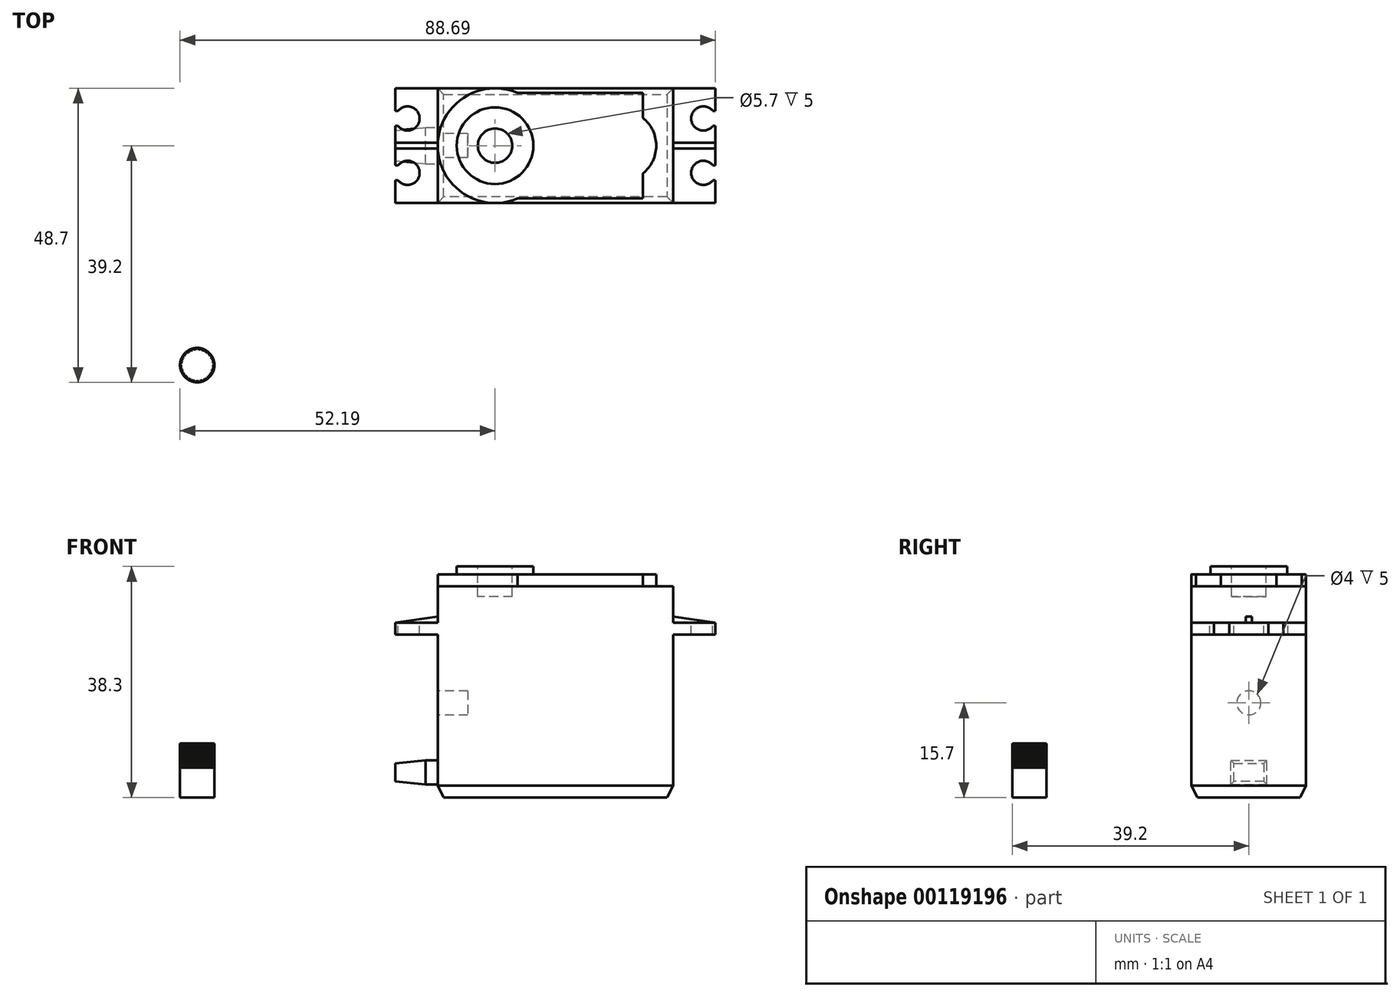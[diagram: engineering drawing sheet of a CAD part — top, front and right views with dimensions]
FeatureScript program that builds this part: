
annotation { "Feature Type Name" : "Feature", "Feature Type Description" : "" }
export const myFeature = defineFeature(function(context is Context, id is Id, definition is map)
    precondition{}
    {
        {
            var Q0;
            Q0=qCreatedBy(makeId("Top.planeOp"),FACE);
            var sketch = newSketch(context, id + "F0", { "sketchPlane" : qUnion([Q0])});
            skLineSegment(sketch, "E0.bottom", {"start": v(19.5, -9.5) * mm, "end": v(-19.5, -9.5) * mm});
            skLineSegment(sketch, "E0.top", {"start": v(19.5, 9.5) * mm, "end": v(-19.5, 9.5) * mm});
            skLineSegment(sketch, "E0.left", {"start": v(19.5, -9.5) * mm, "end": v(19.5, 9.5) * mm});
            skLineSegment(sketch, "E0.right", {"start": v(-19.5, -9.5) * mm, "end": v(-19.5, 9.5) * mm});
            skPoint(sketch, "E0.middle", {"position": v(0, 0) * mm});
            skSolve(sketch);
        }
        {
            var Q0;
            Q0 = qSketchRegion(id + "F0", true);
            extrude(context, id + "F1", {"entities" : qUnion([Q0]), "depth" : 35 * mm});
        }
        {
            var Q0;
            Q0=makeQuery(id+"F1.opExtrude","SWEPT_FACE",FACE,{"disambiguationData":[OSD([sQuery(id+"F0.wireOp",EDGE,"E0.right")])]});
            var sketch = newSketch(context, id + "F2", { "sketchPlane" : qUnion([Q0])});
            skLineSegment(sketch, "E1", {"start": v(-9.5, 29) * mm, "end": v(9.5, 29) * mm});
            skLineSegment(sketch, "E2", {"start": v(-9.5, 27) * mm, "end": v(9.5, 27) * mm});
            skSolve(sketch);
        }
        {
            var Q0;
            {var subQ0=sQuery(id+"F2.wireOp",EDGE,"E1");Q0=makeQuery(id+"F2.imprint","IMPRINT",FACE,{"disambiguationData":[TD([[makeQuery(id+"F2.imprint","IMPRINT",EDGE,{"derivedFrom":subQ0}),-1.0]])]});}
            extrude(context, id + "F3", {"entities" : qUnion([Q0]), "operationType" : NewBodyOperationType.ADD, "depth" : 7 * mm});
        }
        {
            var Q0;
            Q0=makeQuery(id+"F3.opExtrude","SWEPT_FACE",FACE,{"disambiguationData":[OSD([sQuery(id+"F2.wireOp",EDGE,"E1")])]});
            var sketch = newSketch(context, id + "F4", { "sketchPlane" : qUnion([Q0])});
            skLineSegment(sketch, "E3", {"start": v(-26.5, 0.5) * mm, "end": v(-19.5, 0.5) * mm});
            skLineSegment(sketch, "E4", {"start": v(-26.5, -0.5) * mm, "end": v(-19.5, -0.5) * mm});
            skSolve(sketch);
        }
        {
            var Q0;
            {var subQ0=sQuery(id+"F4.wireOp",EDGE,"E3");Q0=makeQuery(id+"F4.imprint","IMPRINT",FACE,{"disambiguationData":[TD([[makeQuery(id+"F4.imprint","IMPRINT",EDGE,{"derivedFrom":subQ0}),-1.0]])]});}
            extrude(context, id + "F5", {"entities" : qUnion([Q0]), "operationType" : NewBodyOperationType.ADD, "depth" : 1 * mm});
        }
        {
            var Q0;
            Q0=makeQuery(id+"F5.opExtrude","SWEPT_FACE",FACE,{"disambiguationData":[OSD([sQuery(id+"F4.wireOp",EDGE,"E4")])]});
            var sketch = newSketch(context, id + "F6", { "sketchPlane" : qUnion([Q0])});
            skLineSegment(sketch, "E5", {"start": v(-26.5, 29) * mm, "end": v(-19.5, 30) * mm});
            skSolve(sketch);
        }
        {
            var Q0;
            Q0=makeQuery(id+"F6.imprint","IMPRINT",FACE,{"disambiguationData":[TD([[makeQuery(id+"F6.imprint","IMPRINT",EDGE,{"derivedFrom":sQuery(id+"F6.wireOp",EDGE,"E5")}),1.0]])]});
            extrude(context, id + "F7", {"entities" : qUnion([Q0]), "operationType" : NewBodyOperationType.REMOVE, "endBound" : BoundingType.UP_TO_NEXT, "oppositeDirection" : true, "depth" : 25 * mm});
        }
        {
            var Q0;
            Q0=makeQuery(id+"F1.opExtrude","CAP_FACE",FACE,{"disambiguationData":[OSD([sQuery(id+"F0.wireOp",EDGE,"E0.bottom"),sQuery(id+"F0.wireOp",EDGE,"E0.top"),sQuery(id+"F0.wireOp",EDGE,"E0.left"),sQuery(id+"F0.wireOp",EDGE,"E0.right")])],"isStart":true});
            chamfer(context, id + "F8", {"entities" : qUnion([Q0]), "chamferType" : ChamferType.TWO_OFFSETS, "width1" : 1 * mm, "oppositeDirection" : false, "width2" : 2 * mm, "tangentPropagation" : true});
        }
        {
            var Q0;
            {var subQ1=sQuery(id+"F0.wireOp",EDGE,"E0.bottom");var subQ2=sQuery(id+"F2.wireOp",EDGE,"E1");Q0=makeQuery(id+"F5.boolean.opBoolean","SPLIT",FACE,{"disambiguationData":[TD([makeQuery(id+"F1.opExtrude","SWEPT_FACE",FACE,{"disambiguationData":[OSD([subQ1])]})])],"derivedFrom":makeQuery(id+"F3.opExtrude","SWEPT_FACE",FACE,{"disambiguationData":[OSD([subQ2])]})});}
            var sketch = newSketch(context, id + "F9", { "sketchPlane" : qUnion([Q0])});
            skArc(sketch, "E6", {"start": v(-26.06, 3.25) * mm, "mid": v(-22.5, 4.5) * mm, "end": v(-26.06, 5.75) * mm});
            skLineSegment(sketch, "E7", {"start": v(-26.06, 5.75) * mm, "end": v(-26.06, 3.25) * mm});
            skLineSegment(sketch, "E8.bottom", {"start": v(-26.06, 5.75) * mm, "end": v(-26.56, 5.75) * mm});
            skLineSegment(sketch, "E8.top", {"start": v(-26.06, 3.25) * mm, "end": v(-26.56, 3.25) * mm});
            skLineSegment(sketch, "E8.right", {"start": v(-26.56, 5.75) * mm, "end": v(-26.56, 3.25) * mm});
            skLineSegment(sketch, "E9.MirrorCS", {"start": v(-26.56, -5.75) * mm, "end": v(-26.56, -3.25) * mm});
            skLineSegment(sketch, "E10.MirrorCS", {"start": v(-26.06, -5.75) * mm, "end": v(-26.56, -5.75) * mm});
            skLineSegment(sketch, "E11.MirrorCS", {"start": v(-26.06, -5.75) * mm, "end": v(-26.06, -3.25) * mm});
            skLineSegment(sketch, "E12.MirrorCS", {"start": v(-26.06, -3.25) * mm, "end": v(-26.56, -3.25) * mm});
            skArc(sketch, "E13.MirrorCS", {"start": v(-26.06, -3.25) * mm, "mid": v(-22.5, -4.5) * mm, "end": v(-26.06, -5.75) * mm});
            skSolve(sketch);
        }
        {
            var Q0;
            Q0=makeQuery(id+"F9.imprint","IMPRINT",FACE,{"disambiguationData":[TD([[makeQuery(id+"F9.imprint","IMPRINT",EDGE,{"derivedFrom":sQuery(id+"F9.wireOp",EDGE,"E8.bottom")}),1.0]])]});
            var Q1;
            Q1=makeQuery(id+"F9.imprint","IMPRINT",FACE,{"disambiguationData":[TD([[makeQuery(id+"F9.imprint","IMPRINT",EDGE,{"derivedFrom":sQuery(id+"F9.wireOp",EDGE,"E6")}),1.0]])]});
            var Q2;
            {var subQ1=sQuery(id+"F9.wireOp",EDGE,"E11.MirrorCS");Q2=makeQuery(id+"F9.imprint","IMPRINT",FACE,{"disambiguationData":[TD([[makeQuery(id+"F9.imprint","IMPRINT",EDGE,{"derivedFrom":subQ1}),1.0]])]});}
            var Q3;
            Q3=makeQuery(id+"F9.imprint","IMPRINT",FACE,{"disambiguationData":[TD([[makeQuery(id+"F9.imprint","IMPRINT",EDGE,{"derivedFrom":sQuery(id+"F9.wireOp",EDGE,"E11.MirrorCS")}),-1.0]])]});
            extrude(context, id + "F10", {"entities" : qUnion([Q0, Q1, Q2, Q3]), "operationType" : NewBodyOperationType.REMOVE, "endBound" : BoundingType.UP_TO_NEXT, "oppositeDirection" : true, "depth" : 25 * mm});
        }
        {
            var Q0;
            Q0=makeQuery(id+"F1.opExtrude","SWEPT_BODY",BODY,{"disambiguationData":[OSD([sQuery(id+"F0.wireOp",EDGE,"E0.bottom"),sQuery(id+"F0.wireOp",EDGE,"E0.top"),sQuery(id+"F0.wireOp",EDGE,"E0.left"),sQuery(id+"F0.wireOp",EDGE,"E0.right")])]});
            var Q1;
            Q1=qCreatedBy(makeId("Right.planeOp"),FACE);
            mirror(context, id + "F11", {"operationType" : NewBodyOperationType.ADD, "entities" : qUnion([Q0]), "mirrorPlane" : qUnion([Q1])});
        }
        {
            var Q0;
            {var subQ1=sQuery(id+"F0.wireOp",EDGE,"E0.right");Q0=makeQuery(id+"F3.boolean.opBoolean","SPLIT",FACE,{"disambiguationData":[TD([makeQuery(id+"F3.opExtrude","SWEPT_FACE",FACE,{"disambiguationData":[OSD([sQuery(id+"F2.wireOp",EDGE,"E2")])]})])],"derivedFrom":makeQuery(id+"F1.opExtrude","SWEPT_FACE",FACE,{"disambiguationData":[OSD([subQ1])]})});}
            var sketch = newSketch(context, id + "F12", { "sketchPlane" : qUnion([Q0])});
            skLineSegment(sketch, "E14.bottom", {"start": v(3, 2.2) * mm, "end": v(-3, 2.2) * mm});
            skLineSegment(sketch, "E14.top", {"start": v(3, 6.2) * mm, "end": v(-3, 6.2) * mm});
            skLineSegment(sketch, "E14.left", {"start": v(3, 2.2) * mm, "end": v(3, 6.2) * mm});
            skLineSegment(sketch, "E14.right", {"start": v(-3, 2.2) * mm, "end": v(-3, 6.2) * mm});
            skPoint(sketch, "E14.middle", {"position": v(0, 4.2) * mm});
            skCircle(sketch, "E15", {"center": v(0, 15.7) * mm, "radius": 2 * mm});
            skSolve(sketch);
        }
        {
            var Q0;
            Q0=makeQuery(id+"F12.imprint","IMPRINT",FACE,{"disambiguationData":[TD([[makeQuery(id+"F12.imprint","IMPRINT",EDGE,{"derivedFrom":sQuery(id+"F12.wireOp",EDGE,"E14.bottom")}),-1.0]])]});
            extrude(context, id + "F13", {"entities" : qUnion([Q0]), "operationType" : NewBodyOperationType.ADD, "depth" : 7 * mm});
        }
        {
            var Q0;
            Q0=makeQuery(id+"F12.imprint","IMPRINT",FACE,{"disambiguationData":[TD([[makeQuery(id+"F12.imprint","IMPRINT",EDGE,{"derivedFrom":sQuery(id+"F12.wireOp",EDGE,"E15")}),1.0]])]});
            extrude(context, id + "F14", {"entities" : qUnion([Q0]), "operationType" : NewBodyOperationType.REMOVE, "oppositeDirection" : true, "depth" : 5 * mm});
        }
        {
            var Q0;
            Q0=makeQuery(id+"F13.opExtrude","CAP_FACE",FACE,{"disambiguationData":[OSD([sQuery(id+"F12.wireOp",EDGE,"E14.bottom"),sQuery(id+"F12.wireOp",EDGE,"E14.top"),sQuery(id+"F12.wireOp",EDGE,"E14.left"),sQuery(id+"F12.wireOp",EDGE,"E14.right")])],"isStart":false});
            chamfer(context, id + "F15", {"entities" : qUnion([Q0]), "chamferType" : ChamferType.TWO_OFFSETS, "width1" : 5 * mm, "oppositeDirection" : false, "width2" : 0.5 * mm, "tangentPropagation" : true});
        }
        {
            var Q0;
            Q0=makeQuery(id+"F1.opExtrude","CAP_FACE",FACE,{"disambiguationData":[OSD([sQuery(id+"F0.wireOp",EDGE,"E0.bottom"),sQuery(id+"F0.wireOp",EDGE,"E0.top"),sQuery(id+"F0.wireOp",EDGE,"E0.left"),sQuery(id+"F0.wireOp",EDGE,"E0.right")])],"isStart":false});
            var sketch = newSketch(context, id + "F16", { "sketchPlane" : qUnion([Q0])});
            skCircle(sketch, "E16", {"center": v(-10, 0) * mm, "radius": 9.5 * mm});
            skPoint(sketch, "E16.first.point", {"position": v(-10, 9.5) * mm});
            skPoint(sketch, "E16.second.point", {"position": v(-19.5, 0) * mm});
            skPoint(sketch, "E16.third.point", {"position": v(-10, -9.5) * mm});
            skLineSegment(sketch, "E17", {"start": v(14.5, 8.75) * mm, "end": v(14.5, -8.75) * mm});
            skLineSegment(sketch, "E18", {"start": v(14.5, -8.75) * mm, "end": v(-6.3, -8.75) * mm});
            skLineSegment(sketch, "E19", {"start": v(14.5, 8.75) * mm, "end": v(-6.3, 8.75) * mm});
            skCircle(sketch, "E20", {"center": v(10.8, 0) * mm, "radius": 5.9 * mm});
            skPoint(sketch, "E20.first.point", {"position": v(14.5, 4.6) * mm});
            skPoint(sketch, "E20.second.point", {"position": v(14.5, -4.6) * mm});
            skPoint(sketch, "E20.third.point", {"position": v(16.7, 0) * mm});
            skPoint(sketch, "E20.third.point.positionSnap0", {"position": v(19.5, 0) * mm});
            skCircle(sketch, "E21", {"center": v(-10, 0) * mm, "radius": 6.35 * mm});
            skSolve(sketch);
        }
        {
            var Q0;
            {var subQ0=sQuery(id+"F16.wireOp",EDGE,"E16");var subQ5=makeQuery(id+"F16.imprint","INTERSECT",VERTEX,{"derivedFrom":[subQ0,sQuery(id+"F16.wireOp",EDGE,"E19")]});Q0=makeQuery(id+"F16.imprint","IMPRINT",FACE,{"disambiguationData":[TD([[makeQuery(id+"F16.imprint","IMPRINT",EDGE,{"disambiguationData":[TD([[subQ5,-1.0]])],"derivedFrom":subQ0}),1.0]])]});}
            var Q1;
            {var subQ0=sQuery(id+"F16.wireOp",EDGE,"E18");Q1=makeQuery(id+"F16.imprint","IMPRINT",FACE,{"disambiguationData":[TD([[makeQuery(id+"F16.imprint","IMPRINT",EDGE,{"derivedFrom":subQ0}),-1.0]])]});}
            var Q2;
            {var subQ0=sQuery(id+"F16.wireOp",EDGE,"E20");var subQ1=sQuery(id+"F16.wireOp",EDGE,"E17");var subQ2=makeQuery(id+"F16.imprint","INTERSECT",VERTEX,{"disambiguationData":[OD(0.0)],"derivedFrom":[subQ1,subQ0]});Q2=makeQuery(id+"F16.imprint","IMPRINT",FACE,{"disambiguationData":[TD([[makeQuery(id+"F16.imprint","IMPRINT",EDGE,{"disambiguationData":[TD([[subQ2,-1.0]])],"derivedFrom":subQ1}),-1.0]])]});}
            var Q3;
            {var subQ0=sQuery(id+"F16.wireOp",EDGE,"E20");var subQ1=sQuery(id+"F16.wireOp",EDGE,"E17");var subQ2=makeQuery(id+"F16.imprint","INTERSECT",VERTEX,{"disambiguationData":[OD(0.0)],"derivedFrom":[subQ1,subQ0]});Q3=makeQuery(id+"F16.imprint","IMPRINT",FACE,{"disambiguationData":[TD([[makeQuery(id+"F16.imprint","IMPRINT",EDGE,{"disambiguationData":[TD([[subQ2,-1.0]])],"derivedFrom":subQ1}),1.0]])]});}
            extrude(context, id + "F17", {"entities" : qUnion([Q0, Q1, Q2, Q3]), "operationType" : NewBodyOperationType.ADD, "depth" : 2 * mm});
        }
        {
            var Q0;
            Q0=makeQuery(id+"F17.boolean.opBoolean","SPLIT",FACE,{"disambiguationData":[TD([makeQuery(id+"F17.opExtrude","SWEPT_FACE",FACE,{"disambiguationData":[OSD([sQuery(id+"F16.wireOp",EDGE,"E21")])]})])],"derivedFrom":makeQuery(id+"F1.opExtrude","CAP_FACE",FACE,{"disambiguationData":[OSD([sQuery(id+"F0.wireOp",EDGE,"E0.bottom"),sQuery(id+"F0.wireOp",EDGE,"E0.top"),sQuery(id+"F0.wireOp",EDGE,"E0.left"),sQuery(id+"F0.wireOp",EDGE,"E0.right")])],"isStart":false})});
            extrude(context, id + "F18", {"entities" : qUnion([Q0]), "operationType" : NewBodyOperationType.ADD, "depth" : 3.3 * mm});
        }
        {
            var Q0;
            Q0=makeQuery(id+"F18.opExtrude","CAP_FACE",FACE,{"disambiguationData":[OSD([sQuery(id+"F0.wireOp",EDGE,"E0.bottom"),sQuery(id+"F0.wireOp",EDGE,"E0.top"),sQuery(id+"F0.wireOp",EDGE,"E0.left"),sQuery(id+"F0.wireOp",EDGE,"E0.right")])],"isStart":false});
            var sketch = newSketch(context, id + "F19", { "sketchPlane" : qUnion([Q0])});
            skCircle(sketch, "E22", {"center": v(-10, 0) * mm, "radius": 2.85 * mm});
            skSolve(sketch);
        }
        {
            var Q0;
            Q0 = qSketchRegion(id + "F19", true);
            extrude(context, id + "F20", {"entities" : qUnion([Q0]), "operationType" : NewBodyOperationType.REMOVE, "oppositeDirection" : true, "depth" : 5 * mm});
        }
        {
            var Q0;
            Q0=qCreatedBy(makeId("Top.planeOp"),FACE);
            var sketch = newSketch(context, id + "F21", { "sketchPlane" : qUnion([Q0])});
            skCircle(sketch, "E23", {"center": v(-59.34, -36.35) * mm, "radius": 2.85 * mm});
            skSolve(sketch);
        }
        {
            var Q0;
            Q0 = qSketchRegion(id + "F21", true);
            extrude(context, id + "F22", {"entities" : qUnion([Q0]), "depth" : 5 * mm});
        }
        {
            var Q0;
            Q0=makeQuery(id+"F22.opExtrude","CAP_FACE",FACE,{"disambiguationData":[OSD([sQuery(id+"F21.wireOp",EDGE,"E23")])],"isStart":false});
            var sketch = newSketch(context, id + "F23", { "sketchPlane" : qUnion([Q0])});
            skArc(sketch, "E24", {"start": v(-60.84, -34.29) * mm, "mid": v(-60.84, -34.29) * mm, "end": v(-60.84, -34.29) * mm});
            skLineSegment(sketch, "E25", {"start": v(-59.66, -33.82) * mm, "end": v(-59.34, -33.5) * mm});
            skLineSegment(sketch, "E26", {"start": v(-59.34, -33.5) * mm, "end": v(-59.02, -33.82) * mm});
            skLineSegment(sketch, "E27.1.0", {"start": v(-60.28, -33.98) * mm, "end": v(-60.05, -33.59) * mm});
            skLineSegment(sketch, "E27.1.1", {"start": v(-60.05, -33.59) * mm, "end": v(-59.66, -33.82) * mm});
            skLineSegment(sketch, "E27.2.0", {"start": v(-60.84, -34.29) * mm, "end": v(-60.71, -33.85) * mm});
            skLineSegment(sketch, "E27.2.1", {"start": v(-60.71, -33.85) * mm, "end": v(-60.28, -33.98) * mm});
            skLineSegment(sketch, "E27.3.0", {"start": v(-61.3, -34.72) * mm, "end": v(-61.3, -34.27) * mm});
            skLineSegment(sketch, "E27.3.1", {"start": v(-61.3, -34.27) * mm, "end": v(-60.84, -34.29) * mm});
            skLineSegment(sketch, "E27.4.0", {"start": v(-61.65, -35.26) * mm, "end": v(-61.75, -34.82) * mm});
            skLineSegment(sketch, "E27.4.1", {"start": v(-61.75, -34.82) * mm, "end": v(-61.3, -34.72) * mm});
            skLineSegment(sketch, "E27.5.0", {"start": v(-61.85, -35.87) * mm, "end": v(-62.05, -35.47) * mm});
            skLineSegment(sketch, "E27.5.1", {"start": v(-62.05, -35.47) * mm, "end": v(-61.65, -35.26) * mm});
            skLineSegment(sketch, "E27.6.0", {"start": v(-61.89, -36.5) * mm, "end": v(-62.19, -36.17) * mm});
            skLineSegment(sketch, "E27.6.1", {"start": v(-62.19, -36.17) * mm, "end": v(-61.85, -35.87) * mm});
            skLineSegment(sketch, "E27.7.0", {"start": v(-61.77, -37.14) * mm, "end": v(-62.14, -36.88) * mm});
            skLineSegment(sketch, "E27.7.1", {"start": v(-62.14, -36.88) * mm, "end": v(-61.89, -36.5) * mm});
            skLineSegment(sketch, "E27.8.0", {"start": v(-61.5, -37.72) * mm, "end": v(-61.92, -37.56) * mm});
            skLineSegment(sketch, "E27.8.1", {"start": v(-61.92, -37.56) * mm, "end": v(-61.77, -37.14) * mm});
            skLineSegment(sketch, "E27.9.0", {"start": v(-61.09, -38.2) * mm, "end": v(-61.54, -38.17) * mm});
            skLineSegment(sketch, "E27.9.1", {"start": v(-61.54, -38.17) * mm, "end": v(-61.5, -37.71) * mm});
            skLineSegment(sketch, "E27.10.0", {"start": v(-60.57, -38.58) * mm, "end": v(-61.02, -38.65) * mm});
            skLineSegment(sketch, "E27.10.1", {"start": v(-61.02, -38.65) * mm, "end": v(-61.09, -38.2) * mm});
            skLineSegment(sketch, "E27.11.0", {"start": v(-59.98, -38.82) * mm, "end": v(-60.4, -39) * mm});
            skLineSegment(sketch, "E27.11.1", {"start": v(-60.4, -39) * mm, "end": v(-60.57, -38.58) * mm});
            skLineSegment(sketch, "E27.12.0", {"start": v(-59.34, -38.9) * mm, "end": v(-59.7, -39.18) * mm});
            skLineSegment(sketch, "E27.12.1", {"start": v(-59.7, -39.18) * mm, "end": v(-59.98, -38.82) * mm});
            skLineSegment(sketch, "E27.13.0", {"start": v(-58.7, -38.82) * mm, "end": v(-58.98, -39.18) * mm});
            skLineSegment(sketch, "E27.13.1", {"start": v(-58.98, -39.18) * mm, "end": v(-59.34, -38.9) * mm});
            skLineSegment(sketch, "E27.14.0", {"start": v(-58.11, -38.58) * mm, "end": v(-58.3, -39) * mm});
            skLineSegment(sketch, "E27.14.1", {"start": v(-58.3, -39) * mm, "end": v(-58.7, -38.82) * mm});
            skLineSegment(sketch, "E27.15.0", {"start": v(-57.6, -38.2) * mm, "end": v(-57.67, -38.65) * mm});
            skLineSegment(sketch, "E27.15.1", {"start": v(-57.67, -38.65) * mm, "end": v(-58.11, -38.58) * mm});
            skLineSegment(sketch, "E27.16.0", {"start": v(-57.19, -37.71) * mm, "end": v(-57.15, -38.17) * mm});
            skLineSegment(sketch, "E27.16.1", {"start": v(-57.15, -38.17) * mm, "end": v(-57.6, -38.2) * mm});
            skLineSegment(sketch, "E27.17.0", {"start": v(-56.92, -37.14) * mm, "end": v(-56.76, -37.56) * mm});
            skLineSegment(sketch, "E27.17.1", {"start": v(-56.76, -37.56) * mm, "end": v(-57.19, -37.72) * mm});
            skLineSegment(sketch, "E27.18.0", {"start": v(-56.8, -36.5) * mm, "end": v(-56.54, -36.88) * mm});
            skLineSegment(sketch, "E27.18.1", {"start": v(-56.54, -36.88) * mm, "end": v(-56.92, -37.14) * mm});
            skLineSegment(sketch, "E27.19.0", {"start": v(-56.84, -35.87) * mm, "end": v(-56.5, -36.17) * mm});
            skLineSegment(sketch, "E27.19.1", {"start": v(-56.5, -36.17) * mm, "end": v(-56.8, -36.5) * mm});
            skLineSegment(sketch, "E27.20.0", {"start": v(-57.03, -35.26) * mm, "end": v(-56.63, -35.47) * mm});
            skLineSegment(sketch, "E27.20.1", {"start": v(-56.63, -35.47) * mm, "end": v(-56.84, -35.87) * mm});
            skLineSegment(sketch, "E27.21.0", {"start": v(-57.38, -34.72) * mm, "end": v(-56.94, -34.82) * mm});
            skLineSegment(sketch, "E27.21.1", {"start": v(-56.94, -34.82) * mm, "end": v(-57.03, -35.26) * mm});
            skLineSegment(sketch, "E27.22.0", {"start": v(-57.84, -34.29) * mm, "end": v(-57.4, -34.27) * mm});
            skLineSegment(sketch, "E27.22.1", {"start": v(-57.4, -34.27) * mm, "end": v(-57.38, -34.72) * mm});
            skLineSegment(sketch, "E27.23.0", {"start": v(-58.4, -33.98) * mm, "end": v(-57.97, -33.85) * mm});
            skLineSegment(sketch, "E27.23.1", {"start": v(-57.97, -33.85) * mm, "end": v(-57.84, -34.29) * mm});
            skLineSegment(sketch, "E27.24.0", {"start": v(-59.02, -33.82) * mm, "end": v(-58.63, -33.59) * mm});
            skLineSegment(sketch, "E27.24.1", {"start": v(-58.63, -33.59) * mm, "end": v(-58.4, -33.98) * mm});
            skArc(sketch, "E28.trimOffspring", {"start": v(-60.28, -33.98) * mm, "mid": v(-60.28, -33.98) * mm, "end": v(-60.28, -33.98) * mm});
            skArc(sketch, "E29.trimOffspring", {"start": v(-59.02, -33.82) * mm, "mid": v(-59.02, -33.82) * mm, "end": v(-59.02, -33.82) * mm});
            skArc(sketch, "E30.trimOffspring", {"start": v(-57.84, -34.29) * mm, "mid": v(-57.84, -34.29) * mm, "end": v(-57.84, -34.29) * mm});
            skArc(sketch, "E31.trimOffspring", {"start": v(-61.3, -34.72) * mm, "mid": v(-61.3, -34.72) * mm, "end": v(-61.3, -34.72) * mm});
            skArc(sketch, "E32.trimOffspring", {"start": v(-61.65, -35.26) * mm, "mid": v(-61.65, -35.26) * mm, "end": v(-61.65, -35.26) * mm});
            skArc(sketch, "E33.trimOffspring", {"start": v(-61.85, -35.87) * mm, "mid": v(-61.85, -35.87) * mm, "end": v(-61.85, -35.87) * mm});
            skArc(sketch, "E34.trimOffspring", {"start": v(-61.89, -36.5) * mm, "mid": v(-61.89, -36.5) * mm, "end": v(-61.89, -36.5) * mm});
            skArc(sketch, "E35.trimOffspring", {"start": v(-61.77, -37.14) * mm, "mid": v(-61.77, -37.14) * mm, "end": v(-61.77, -37.14) * mm});
            skArc(sketch, "E36.trimOffspring", {"start": v(-61.5, -37.71) * mm, "mid": v(-61.5, -37.72) * mm, "end": v(-61.5, -37.72) * mm});
            skArc(sketch, "E37.trimOffspring", {"start": v(-61.09, -38.2) * mm, "mid": v(-61.09, -38.2) * mm, "end": v(-61.09, -38.2) * mm});
            skArc(sketch, "E38.trimOffspring", {"start": v(-60.57, -38.58) * mm, "mid": v(-60.57, -38.58) * mm, "end": v(-60.57, -38.58) * mm});
            skArc(sketch, "E39.trimOffspring", {"start": v(-59.98, -38.82) * mm, "mid": v(-59.98, -38.82) * mm, "end": v(-59.98, -38.82) * mm});
            skArc(sketch, "E40.trimOffspring", {"start": v(-59.34, -38.9) * mm, "mid": v(-59.34, -38.9) * mm, "end": v(-59.34, -38.9) * mm});
            skArc(sketch, "E41.trimOffspring", {"start": v(-58.7, -38.82) * mm, "mid": v(-58.7, -38.82) * mm, "end": v(-58.7, -38.82) * mm});
            skArc(sketch, "E42.trimOffspring", {"start": v(-58.11, -38.58) * mm, "mid": v(-58.11, -38.58) * mm, "end": v(-58.11, -38.58) * mm});
            skArc(sketch, "E43.trimOffspring", {"start": v(-57.6, -38.2) * mm, "mid": v(-57.6, -38.2) * mm, "end": v(-57.6, -38.2) * mm});
            skArc(sketch, "E44.trimOffspring", {"start": v(-57.19, -37.72) * mm, "mid": v(-57.19, -37.72) * mm, "end": v(-57.19, -37.71) * mm});
            skArc(sketch, "E45.trimOffspring", {"start": v(-56.92, -37.14) * mm, "mid": v(-56.92, -37.14) * mm, "end": v(-56.92, -37.14) * mm});
            skArc(sketch, "E46.trimOffspring", {"start": v(-56.8, -36.5) * mm, "mid": v(-56.8, -36.5) * mm, "end": v(-56.8, -36.5) * mm});
            skArc(sketch, "E47.trimOffspring", {"start": v(-56.84, -35.87) * mm, "mid": v(-56.84, -35.87) * mm, "end": v(-56.84, -35.87) * mm});
            skArc(sketch, "E48.trimOffspring", {"start": v(-57.03, -35.26) * mm, "mid": v(-57.03, -35.26) * mm, "end": v(-57.03, -35.26) * mm});
            skArc(sketch, "E49.trimOffspring", {"start": v(-57.38, -34.72) * mm, "mid": v(-57.38, -34.72) * mm, "end": v(-57.38, -34.72) * mm});
            skSolve(sketch);
        }
        {
            var Q0;
            Q0 = qSketchRegion(id + "F23", true);
            extrude(context, id + "F24", {"entities" : qUnion([Q0]), "operationType" : NewBodyOperationType.ADD, "depth" : 4 * mm});
        }
    });
